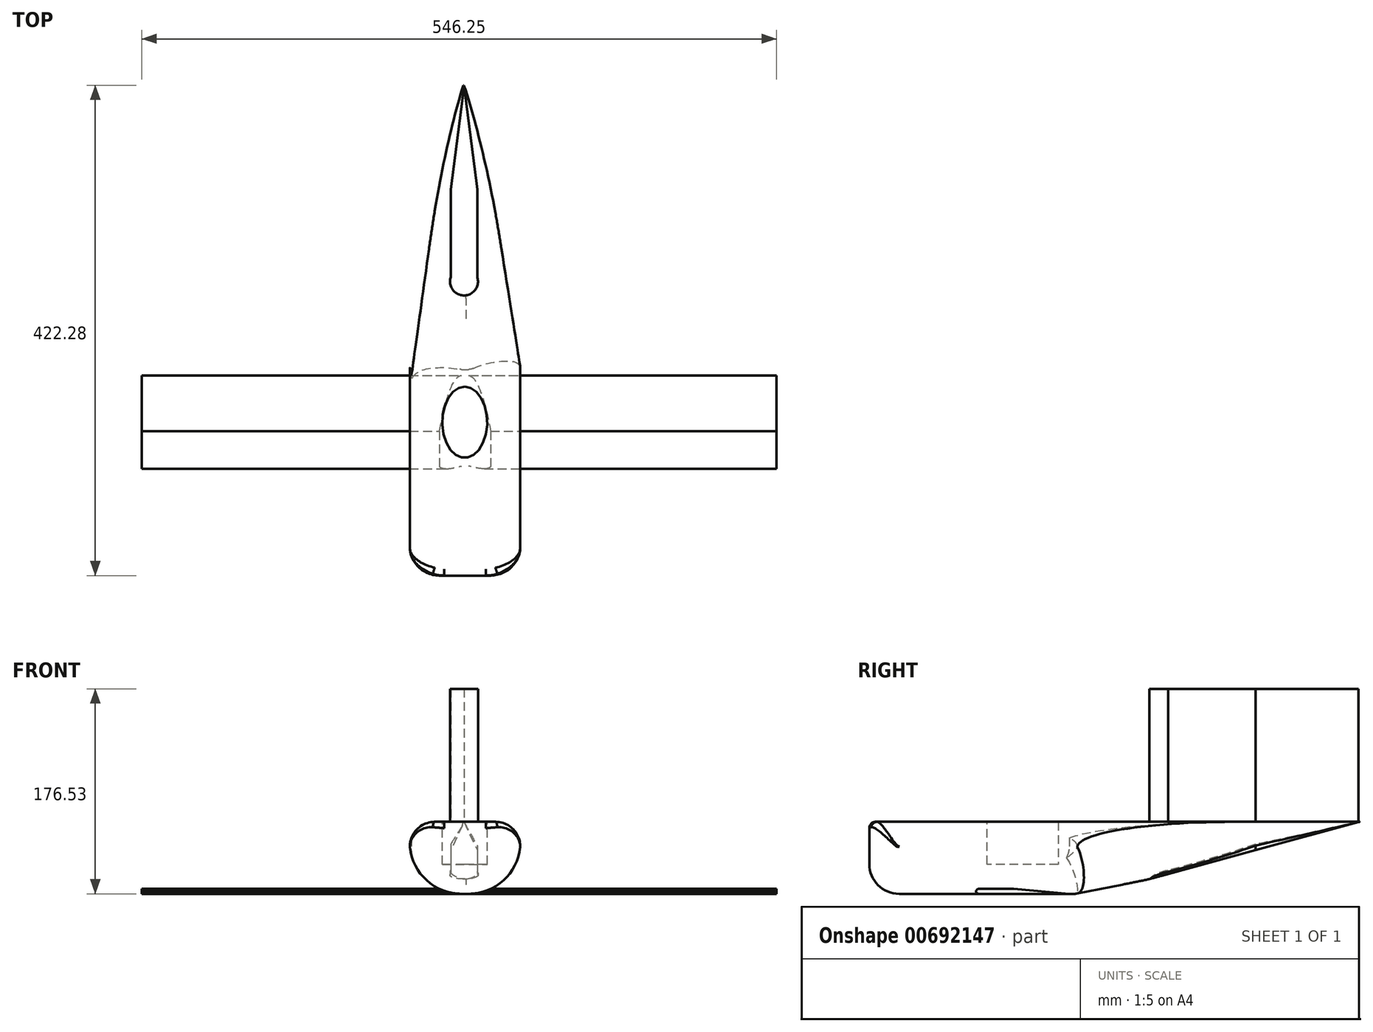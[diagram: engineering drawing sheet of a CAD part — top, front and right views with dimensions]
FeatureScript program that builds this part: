
annotation { "Feature Type Name" : "Feature", "Feature Type Description" : "" }
export const myFeature = defineFeature(function(context is Context, id is Id, definition is map)
    precondition{}
    {
        {
            var Q0;
            Q0=qCreatedBy(makeId("Front.planeOp"),FACE);
            var sketch = newSketch(context, id + "F0", { "sketchPlane" : qUnion([Q0])});
            skLineSegment(sketch, "E0.bottom", {"start": v(-140.06, 4.25) * mm, "end": v(143.3, 4.25) * mm});
            skLineSegment(sketch, "E0.top", {"start": v(-140.06, 0) * mm, "end": v(143.3, 0) * mm});
            skLineSegment(sketch, "E0.left", {"start": v(-140.06, 4.25) * mm, "end": v(-140.06, 0) * mm});
            skLineSegment(sketch, "E0.right", {"start": v(143.3, 4.25) * mm, "end": v(143.3, 0) * mm});
            skSolve(sketch);
        }
        {
            var Q0;
            Q0 = qSketchRegion(id + "F0", true);
            extrude(context, id + "F1", {"entities" : qUnion([Q0]), "endBound" : BoundingType.SYMMETRIC, "depth" : 80.26 * mm, "offsetDistance" : 25.4 * mm});
        }
        {
            var Q0;
            Q0=qCreatedBy(makeId("Right.planeOp"),FACE);
            var sketch = newSketch(context, id + "F2", { "sketchPlane" : qUnion([Q0])});
            skLineSegment(sketch, "E1", {"start": v(40.24, 0) * mm, "end": v(-12.84, 4.7) * mm});
            skLineSegment(sketch, "E2", {"start": v(-12.84, 4.7) * mm, "end": v(29.42, 13.5) * mm});
            skLineSegment(sketch, "E3", {"start": v(29.42, 13.5) * mm, "end": v(57.99, 4.7) * mm});
            skLineSegment(sketch, "E4", {"start": v(57.99, 4.7) * mm, "end": v(40.24, 0) * mm});
            skSolve(sketch);
        }
        {
            var Q0;
            Q0 = qSketchRegion(id + "F2", true);
            extrude(context, id + "F3", {"entities" : qUnion([Q0]), "operationType" : NewBodyOperationType.REMOVE, "endBound" : BoundingType.SYMMETRIC, "depth" : 467.36 * mm, "offsetDistance" : 25.4 * mm});
        }
        {
            var Q0;
            Q0=makeQuery(id+"F1.opExtrude","CAP_EDGE",EDGE,{"disambiguationData":[OSD([sQuery(id+"F0.wireOp",EDGE,"E0.bottom")])],"isStart":false});
            var Q1;
            Q1=makeQuery(id+"F1.opExtrude","CAP_EDGE",EDGE,{"disambiguationData":[OSD([sQuery(id+"F0.wireOp",EDGE,"E0.top")])],"isStart":false});
            fillet(context, id + "F4", {"entities" : qUnion([Q0, Q1]), "radius" : 2.45 * mm, "tangentPropagation" : true, "allowEdgeOverflow" : false});
        }
        {
            var Q0;
            Q0=makeQuery(id+"F1.opExtrude","SWEPT_FACE",FACE,{"disambiguationData":[OSD([sQuery(id+"F0.wireOp",EDGE,"E0.left")])]});
            var Q1;
            Q1=makeQuery(id+"F1.opExtrude","SWEPT_FACE",FACE,{"disambiguationData":[OSD([sQuery(id+"F0.wireOp",EDGE,"E0.right")])]});
            extrude(context, id + "F5", {"entities" : qUnion([Q0, Q1]), "operationType" : NewBodyOperationType.ADD, "depth" : 262.9 * mm, "offsetDistance" : 25.4 * mm});
        }
        {
            var Q0;
            Q0=qCreatedBy(makeId("Top.planeOp"),FACE);
            var sketch = newSketch(context, id + "F6", { "sketchPlane" : qUnion([Q0])});
            skLineSegment(sketch, "E5.bottom", {"start": v(-172.3, 124.44) * mm, "end": v(-77.15, 124.44) * mm});
            skLineSegment(sketch, "E5.top", {"start": v(-172.3, -131.97) * mm, "end": v(-77.15, -131.97) * mm});
            skLineSegment(sketch, "E5.left", {"start": v(-172.3, 124.44) * mm, "end": v(-172.3, -131.97) * mm});
            skLineSegment(sketch, "E5.right", {"start": v(-77.15, 124.44) * mm, "end": v(-77.15, -131.97) * mm});
            skSolve(sketch);
        }
        {
            var Q0;
            Q0 = qSketchRegion(id + "F6", true);
            extrude(context, id + "F7", {"entities" : qUnion([Q0]), "operationType" : NewBodyOperationType.ADD, "depth" : 61.98 * mm, "offsetDistance" : 25.4 * mm});
        }
        {
            var Q0;
            Q0=makeQuery(id+"F7.opExtrude","CAP_EDGE",EDGE,{"disambiguationData":[OSD([sQuery(id+"F6.wireOp",EDGE,"E5.right")])],"isStart":false});
            var Q1;
            Q1=makeQuery(id+"F7.opExtrude","CAP_EDGE",EDGE,{"disambiguationData":[OSD([sQuery(id+"F6.wireOp",EDGE,"E5.left")])],"isStart":false});
            fillet(context, id + "F8", {"entities" : qUnion([Q0, Q1]), "radius" : 21.46 * mm, "tangentPropagation" : true, "allowEdgeOverflow" : false});
        }
        {
            var Q0;
            {var subQ1=sQuery(id+"F0.wireOp",EDGE,"E0.top");var subQ3=sQuery(id+"F6.wireOp",EDGE,"E5.right");Q0=makeQuery(id+"F7.boolean.opBoolean","SPLIT",EDGE,{"disambiguationData":[TD([makeQuery(id+"F4.opFillet","BLEND_FACE",FACE,{"disambiguationData":[OSD([subQ1])]})])],"derivedFrom":makeQuery(id+"F7.opExtrude","CAP_EDGE",EDGE,{"disambiguationData":[OSD([subQ3])],"isStart":true})});}
            var Q1;
            {var subQ1=sQuery(id+"F0.wireOp",EDGE,"E0.top");var subQ3=sQuery(id+"F6.wireOp",EDGE,"E5.left");Q1=makeQuery(id+"F7.boolean.opBoolean","SPLIT",EDGE,{"disambiguationData":[TD([makeQuery(id+"F4.opFillet","BLEND_FACE",FACE,{"disambiguationData":[OSD([subQ1])]})])],"derivedFrom":makeQuery(id+"F7.opExtrude","CAP_EDGE",EDGE,{"disambiguationData":[OSD([subQ3])],"isStart":true})});}
            fillet(context, id + "F9", {"entities" : qUnion([Q0, Q1]), "radius" : 44.76 * mm, "tangentPropagation" : true, "allowEdgeOverflow" : false});
        }
        {
            var Q0;
            {var subQ0=sQuery(id+"F6.wireOp",EDGE,"E5.top");var subQ1=makeQuery(id+"F7.opExtrude","SWEPT_FACE",FACE,{"disambiguationData":[OSD([subQ0])]});var subQ3=sQuery(id+"F0.wireOp",EDGE,"E0.top");var subQ4=sQuery(id+"F6.wireOp",EDGE,"E5.right");Q0=makeQuery(id+"F9.opFillet","BLEND_EDGE",EDGE,{"blendedFrom":[makeQuery(id+"F7.boolean.opBoolean","SPLIT",EDGE,{"disambiguationData":[TD([makeQuery(id+"F4.opFillet","BLEND_FACE",FACE,{"disambiguationData":[OSD([subQ3])]})])],"derivedFrom":makeQuery(id+"F7.opExtrude","CAP_EDGE",EDGE,{"disambiguationData":[OSD([subQ4])],"isStart":true})}),subQ1],"blendedInto":[subQ1]});}
            fillet(context, id + "F10", {"entities" : qUnion([Q0]), "radius" : 25.75 * mm, "tangentPropagation" : true, "allowEdgeOverflow" : false});
        }
        {
            var Q0;
            Q0=makeQuery(id+"F7.opExtrude","CAP_EDGE",EDGE,{"disambiguationData":[OSD([sQuery(id+"F6.wireOp",EDGE,"E5.top")])],"isStart":false});
            fillet(context, id + "F11", {"entities" : qUnion([Q0]), "radius" : 5.52 * mm, "tangentPropagation" : true, "allowEdgeOverflow" : false});
        }
        {
            var Q0;
            Q0=qCreatedBy(makeId("Top.planeOp"),FACE);
            var sketch = newSketch(context, id + "F12", { "sketchPlane" : qUnion([Q0])});
            skEllipse(sketch, "E6", {"center": v(-125, 0) * mm, "majorRadius": 30.62 * mm, "minorRadius": 19.38 * mm, "majorAxis": v(0, 1)});
            skSolve(sketch);
        }
        {
            var Q0;
            Q0 = qSketchRegion(id + "F12", true);
            extrude(context, id + "F13", {"entities" : qUnion([Q0]), "operationType" : NewBodyOperationType.REMOVE, "depth" : 113.03 * mm, "offsetDistance" : 25.4 * mm});
        }
        {
            var Q0;
            Q0=makeQuery(id+"F12.imprint","IMPRINT",FACE,{"disambiguationData":[TD([[makeQuery(id+"F12.imprint","IMPRINT",EDGE,{"derivedFrom":sQuery(id+"F12.wireOp",EDGE,"E6")}),1.0]])]});
            extrude(context, id + "F14", {"entities" : qUnion([Q0]), "operationType" : NewBodyOperationType.ADD, "depth" : 25.4 * mm, "offsetDistance" : 25.4 * mm});
        }
        {
            var Q0;
            Q0=makeQuery(id+"F7.opExtrude","SWEPT_FACE",FACE,{"disambiguationData":[OSD([sQuery(id+"F6.wireOp",EDGE,"E5.bottom")])]});
            extrude(context, id + "F15", {"entities" : qUnion([Q0]), "operationType" : NewBodyOperationType.ADD, "depth" : 231.14 * mm, "offsetDistance" : 25.4 * mm});
        }
        {
            var Q0;
            Q0=qCreatedBy(makeId("Top.planeOp"),FACE);
            var sketch = newSketch(context, id + "F16", { "sketchPlane" : qUnion([Q0])});
            skLineSegment(sketch, "E7", {"start": v(-170.85, 40.28) * mm, "end": v(-124.58, 374.47) * mm});
            skLineSegment(sketch, "E8", {"start": v(-126.7, 359.22) * mm, "end": v(-76.6, 43.7) * mm});
            skLineSegment(sketch, "E9", {"start": v(-76.6, 43.7) * mm, "end": v(-31.18, 430.17) * mm});
            skLineSegment(sketch, "E10", {"start": v(-31.18, 430.17) * mm, "end": v(-241.97, 385.6) * mm});
            skLineSegment(sketch, "E11", {"start": v(-241.97, 385.6) * mm, "end": v(-170.85, 40.28) * mm});
            skSolve(sketch);
        }
        {
            var Q0;
            Q0 = qSketchRegion(id + "F16", true);
            extrude(context, id + "F17", {"entities" : qUnion([Q0]), "operationType" : NewBodyOperationType.REMOVE, "depth" : 172.72 * mm, "offsetDistance" : 25.4 * mm});
        }
        {
            var Q0;
            Q0=qCreatedBy(makeId("Right.planeOp"),FACE);
            var sketch = newSketch(context, id + "F18", { "sketchPlane" : qUnion([Q0])});
            skLineSegment(sketch, "E12", {"start": v(45.5, 0) * mm, "end": v(365.17, 62.82) * mm});
            skLineSegment(sketch, "E13", {"start": v(365.17, 62.82) * mm, "end": v(352.9, -28.16) * mm});
            skLineSegment(sketch, "E14", {"start": v(352.9, -28.16) * mm, "end": v(45.5, 0) * mm});
            skSolve(sketch);
        }
        {
            var Q0;
            Q0 = qSketchRegion(id + "F18", true);
            extrude(context, id + "F19", {"entities" : qUnion([Q0]), "operationType" : NewBodyOperationType.REMOVE, "oppositeDirection" : true, "depth" : 299.97 * mm, "offsetDistance" : 25.4 * mm});
        }
        {
            var Q0;
            Q0=makeQuery(id+"F19.boolean.opBoolean","INTERSECT",EDGE,{"derivedFrom":[makeQuery(id+"F17.boolean.opBoolean","COPY",FACE,{"derivedFrom":makeQuery(id+"F17.opExtrude","SWEPT_FACE",FACE,{"disambiguationData":[OSD([sQuery(id+"F16.wireOp",EDGE,"E7")])]})}),makeQuery(id+"F19.opExtrude","SWEPT_FACE",FACE,{"disambiguationData":[OSD([sQuery(id+"F18.wireOp",EDGE,"E12")])]})]});
            var Q1;
            Q1=makeQuery(id+"F19.boolean.opBoolean","INTERSECT",EDGE,{"derivedFrom":[makeQuery(id+"F17.boolean.opBoolean","COPY",FACE,{"derivedFrom":makeQuery(id+"F17.opExtrude","SWEPT_FACE",FACE,{"disambiguationData":[OSD([sQuery(id+"F16.wireOp",EDGE,"E8")])]})}),makeQuery(id+"F19.opExtrude","SWEPT_FACE",FACE,{"disambiguationData":[OSD([sQuery(id+"F18.wireOp",EDGE,"E12")])]})]});
            fillet(context, id + "F20", {"entities" : qUnion([Q0, Q1]), "radius" : 41.33 * mm, "tangentPropagation" : true, "allowEdgeOverflow" : false});
        }
        {
            var Q0;
            Q0=qCreatedBy(makeId("Top.planeOp"),FACE);
            var sketch = newSketch(context, id + "F21", { "sketchPlane" : qUnion([Q0])});
            skArc(sketch, "E15", {"start": v(-137.08, 124.92) * mm, "mid": v(-125.47, 109.23) * mm, "end": v(-114.24, 125.2) * mm});
            skLineSegment(sketch, "E16", {"start": v(-114.24, 125.2) * mm, "end": v(-114.24, 200.72) * mm});
            skLineSegment(sketch, "E17", {"start": v(-137.08, 124.92) * mm, "end": v(-137.08, 200.72) * mm});
            skLineSegment(sketch, "E18", {"start": v(-137.08, 200.72) * mm, "end": v(-125.61, 289.27) * mm});
            skLineSegment(sketch, "E19", {"start": v(-114.24, 200.72) * mm, "end": v(-125.61, 289.27) * mm});
            skSolve(sketch);
        }
        {
            var Q0;
            Q0 = qSketchRegion(id + "F21", true);
            extrude(context, id + "F22", {"entities" : qUnion([Q0]), "operationType" : NewBodyOperationType.ADD, "depth" : 176.53 * mm, "offsetDistance" : 25.4 * mm});
        }
        {
            var Q0;
            Q0=qCreatedBy(makeId("Right.planeOp"),FACE);
            var sketch = newSketch(context, id + "F23", { "sketchPlane" : qUnion([Q0])});
            skLineSegment(sketch, "E20", {"start": v(106.27, 11.93) * mm, "end": v(296.82, 63.75) * mm});
            skLineSegment(sketch, "E21", {"start": v(296.82, 63.75) * mm, "end": v(270.91, -29.02) * mm});
            skLineSegment(sketch, "E22", {"start": v(270.91, -29.02) * mm, "end": v(287.63, -29.02) * mm});
            skLineSegment(sketch, "E23", {"start": v(287.63, -29.02) * mm, "end": v(301.42, 39.93) * mm});
            skLineSegment(sketch, "E24", {"start": v(301.42, 39.93) * mm, "end": v(296.82, 63.75) * mm});
            skLineSegment(sketch, "E25", {"start": v(270.91, -29.02) * mm, "end": v(92.9, -6.87) * mm});
            skLineSegment(sketch, "E26", {"start": v(92.9, -6.87) * mm, "end": v(106.27, 11.93) * mm});
            skSolve(sketch);
        }
        {
            var Q0;
            Q0 = qSketchRegion(id + "F23", true);
            extrude(context, id + "F24", {"entities" : qUnion([Q0]), "operationType" : NewBodyOperationType.REMOVE, "oppositeDirection" : true, "depth" : 229.36 * mm, "offsetDistance" : 25.4 * mm});
        }
    });
